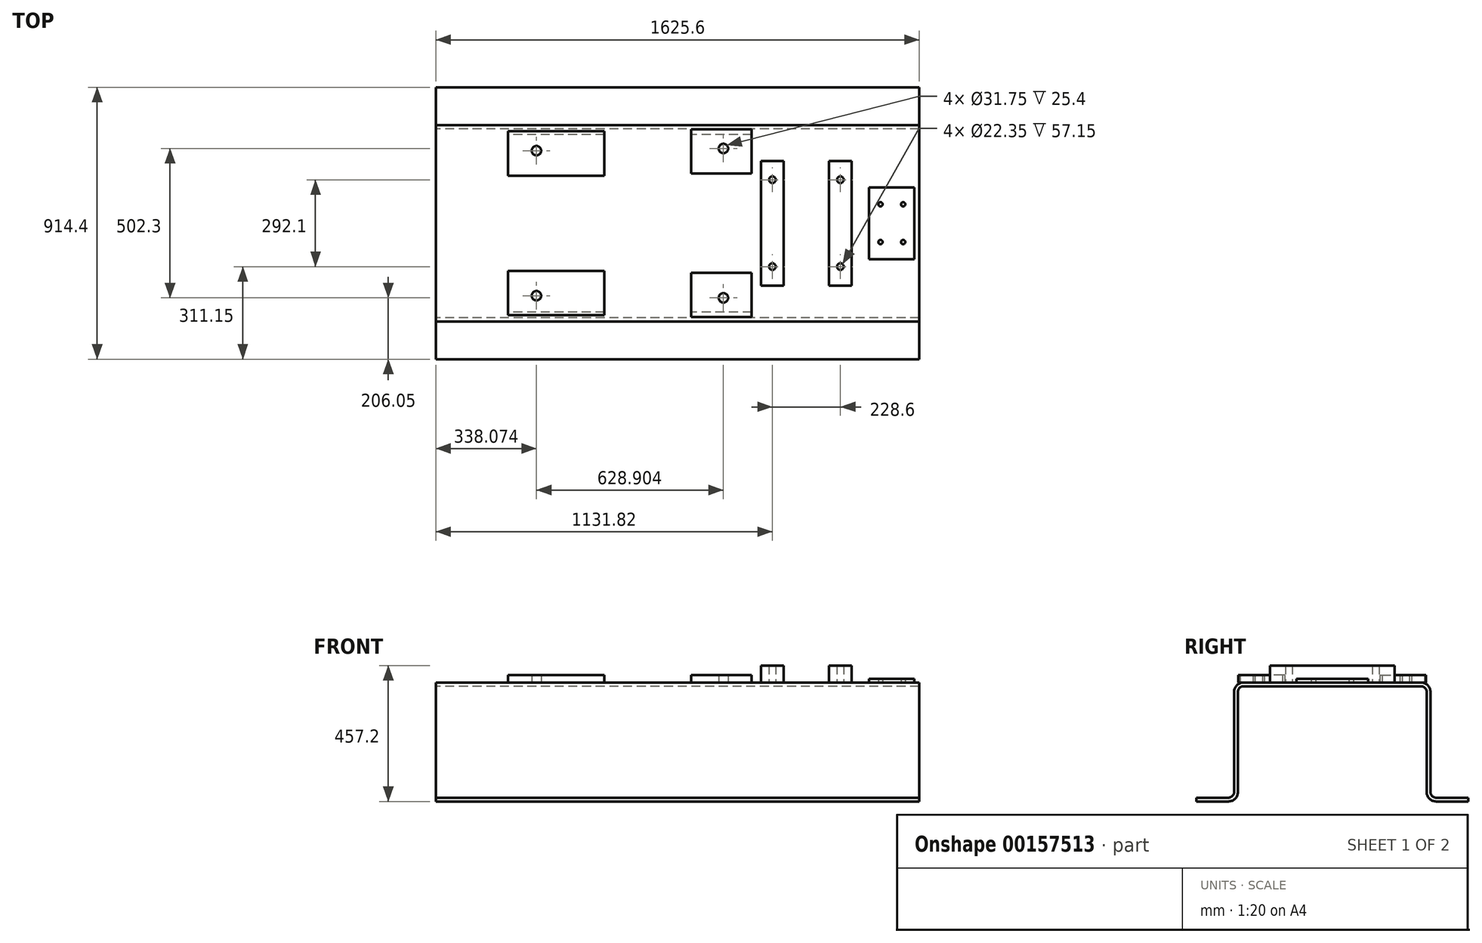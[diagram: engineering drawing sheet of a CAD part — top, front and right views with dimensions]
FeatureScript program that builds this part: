
annotation { "Feature Type Name" : "Feature", "Feature Type Description" : "" }
export const myFeature = defineFeature(function(context is Context, id is Id, definition is map)
    precondition{}
    {
        {
            var Q0;
            Q0=qCreatedBy(makeId("Right.planeOp"),FACE);
            var sketch = newSketch(context, id + "F0", { "sketchPlane" : qUnion([Q0])});
            skLineSegment(sketch, "E0", {"start": v(349.25, 0) * mm, "end": v(457.2, 0) * mm});
            skLineSegment(sketch, "E1.0", {"start": v(349.25, 12.7) * mm, "end": v(457.2, 12.7) * mm});
            skLineSegment(sketch, "E2.0", {"start": v(0, 400.05) * mm, "end": v(298.45, 400.05) * mm});
            skLineSegment(sketch, "E3", {"start": v(0, -167.8) * mm, "end": v(0, 400.05) * mm, "construction": true});
            skLineSegment(sketch, "E4.0", {"start": v(0, 387.35) * mm, "end": v(298.45, 387.35) * mm});
            skLineSegment(sketch, "E5.0", {"start": v(330.2, 31.75) * mm, "end": v(330.2, 368.3) * mm});
            skLineSegment(sketch, "E6.0", {"start": v(317.5, 31.75) * mm, "end": v(317.5, 368.3) * mm});
            skArc(sketch, "E7.filletArc", {"start": v(330.2, 31.75) * mm, "mid": v(335.78, 18.28) * mm, "end": v(349.25, 12.7) * mm});
            skArc(sketch, "E8.filletArc", {"start": v(317.5, 368.3) * mm, "mid": v(311.92, 381.77) * mm, "end": v(298.45, 387.35) * mm});
            skArc(sketch, "E9.filletArc", {"start": v(330.2, 368.3) * mm, "mid": v(320.9, 390.75) * mm, "end": v(298.45, 400.05) * mm});
            skPoint(sketch, "E10.newPointA", {"position": v(-457.2, 0) * mm});
            skArc(sketch, "E10.filletArc", {"start": v(317.5, 31.75) * mm, "mid": v(326.8, 9.3) * mm, "end": v(349.25, 0) * mm});
            skLineSegment(sketch, "E11", {"start": v(457.2, 12.7) * mm, "end": v(457.2, 0) * mm});
            skLineSegment(sketch, "E12.MirrorCS", {"start": v(-457.2, 12.7) * mm, "end": v(-457.2, 0) * mm});
            skArc(sketch, "E13.MirrorCS", {"start": v(-330.2, 368.3) * mm, "mid": v(-320.9, 390.75) * mm, "end": v(-298.45, 400.05) * mm});
            skArc(sketch, "E14.MirrorCS", {"start": v(-330.2, 31.75) * mm, "mid": v(-335.78, 18.28) * mm, "end": v(-349.25, 12.7) * mm});
            skArc(sketch, "E15.MirrorCS", {"start": v(-317.5, 368.3) * mm, "mid": v(-311.92, 381.77) * mm, "end": v(-298.45, 387.35) * mm});
            skArc(sketch, "E16.MirrorCS", {"start": v(-317.5, 31.75) * mm, "mid": v(-326.8, 9.3) * mm, "end": v(-349.25, 0) * mm});
            skLineSegment(sketch, "E17.MirrorCS", {"start": v(-349.25, 0) * mm, "end": v(-457.2, 0) * mm});
            skLineSegment(sketch, "E18.MirrorCS", {"start": v(-349.25, 12.7) * mm, "end": v(-457.2, 12.7) * mm});
            skLineSegment(sketch, "E19.MirrorCS", {"start": v(0, 400.05) * mm, "end": v(-298.45, 400.05) * mm});
            skLineSegment(sketch, "E20.MirrorCS", {"start": v(0, 387.35) * mm, "end": v(-298.45, 387.35) * mm});
            skLineSegment(sketch, "E21.MirrorCS", {"start": v(-317.5, 31.75) * mm, "end": v(-317.5, 368.3) * mm});
            skLineSegment(sketch, "E22.MirrorCS", {"start": v(-330.2, 31.75) * mm, "end": v(-330.2, 368.3) * mm});
            skSolve(sketch);
        }
        {
            var Q0;
            Q0=qSketchRegion(id+"F0",true);
            extrude(context, id + "F1", {"entities" : qUnion([Q0]), "endBound" : BoundingType.SYMMETRIC, "depth" : 1625.6 * mm});
        }
        {
            var Q0;
            Q0=makeQuery(id+"F1.opExtrude","SWEPT_FACE",FACE,{"disambiguationData":[OSD([sQuery(id+"F0.wireOp",EDGE,"E2.0"),sQuery(id+"F0.wireOp",EDGE,"E19.MirrorCS")])]});
            var sketch = newSketch(context, id + "F2", { "sketchPlane" : qUnion([Q0])});
            skLineSegment(sketch, "E23.0", {"start": v(812.8, -298.45) * mm, "end": v(812.8, 298.45) * mm, "construction": true});
            skLineSegment(sketch, "E24.0", {"start": v(-1600.2, -987.8) * mm, "end": v(-1600.2, 298.45) * mm, "construction": true});
            skLineSegment(sketch, "E25.0", {"start": v(-1143, -987.8) * mm, "end": v(-1143, 298.45) * mm, "construction": true});
            skLineSegment(sketch, "E26.0", {"start": v(-160.27, -987.8) * mm, "end": v(-160.27, 298.45) * mm, "construction": true});
            skLineSegment(sketch, "E27.0", {"start": v(433.32, -987.8) * mm, "end": v(433.32, 298.45) * mm, "construction": true});
            skLineSegment(sketch, "E28.0", {"start": v(45.97, -987.8) * mm, "end": v(45.97, 298.45) * mm, "construction": true});
            skLineSegment(sketch, "E29.0", {"start": v(249.17, -987.8) * mm, "end": v(249.17, 298.45) * mm, "construction": true});
            skLineSegment(sketch, "E30.0", {"start": v(-246.13, -987.8) * mm, "end": v(-246.13, 298.45) * mm, "construction": true});
            skLineSegment(sketch, "E31.0", {"start": v(-569.98, -987.8) * mm, "end": v(-569.98, 298.45) * mm, "construction": true});
            skLineSegment(sketch, "E32.0", {"start": v(-958.44, -155.44) * mm, "end": v(1000.49, -178.16) * mm, "construction": true});
            skLineSegment(sketch, "E33.0", {"start": v(-960.13, -301.48) * mm, "end": v(998.8, -324.2) * mm, "construction": true});
            skLineSegment(sketch, "E34.bottom", {"start": v(-569.98, -159.94) * mm, "end": v(-246.13, -159.94) * mm});
            skLineSegment(sketch, "E34.top", {"start": v(-569.98, -309.76) * mm, "end": v(-246.13, -309.76) * mm});
            skLineSegment(sketch, "E34.left", {"start": v(-569.98, -159.94) * mm, "end": v(-569.98, -309.76) * mm});
            skLineSegment(sketch, "E34.right", {"start": v(-246.13, -159.94) * mm, "end": v(-246.13, -309.76) * mm});
            skLineSegment(sketch, "E35.bottom", {"start": v(45.97, -167.09) * mm, "end": v(249.17, -167.09) * mm});
            skLineSegment(sketch, "E35.top", {"start": v(45.97, -315.5) * mm, "end": v(249.17, -315.5) * mm});
            skLineSegment(sketch, "E35.left", {"start": v(45.97, -167.09) * mm, "end": v(45.97, -315.5) * mm});
            skLineSegment(sketch, "E35.right", {"start": v(249.17, -167.09) * mm, "end": v(249.17, -315.5) * mm});
            skLineSegment(sketch, "E36.0", {"start": v(-474.73, -987.8) * mm, "end": v(-474.73, 298.45) * mm, "construction": true});
            skLineSegment(sketch, "E37.0", {"start": v(154.18, -987.8) * mm, "end": v(154.18, 298.45) * mm, "construction": true});
            skLineSegment(sketch, "E38.0", {"start": v(-959.4, -238.24) * mm, "end": v(999.53, -260.95) * mm, "construction": true});
            skCircle(sketch, "E39", {"center": v(-474.73, -243.86) * mm, "radius": 15.88 * mm});
            skCircle(sketch, "E40", {"center": v(154.18, -251.15) * mm, "radius": 15.88 * mm});
            skLineSegment(sketch, "E41", {"start": v(-969.18, 0) * mm, "end": v(1017.58, 0) * mm, "construction": true});
            skPoint(sketch, "E41.startSnap0", {"position": v(-812.8, 0) * mm});
            skCircle(sketch, "E42.MirrorC", {"center": v(154.18, 251.15) * mm, "radius": 15.88 * mm});
            skCircle(sketch, "E43.MirrorC", {"center": v(-474.73, 243.86) * mm, "radius": 15.88 * mm});
            skLineSegment(sketch, "E44.MirrorCS", {"start": v(-246.13, 159.94) * mm, "end": v(-246.13, 309.76) * mm});
            skLineSegment(sketch, "E45.MirrorCS", {"start": v(45.97, 167.09) * mm, "end": v(249.17, 167.09) * mm});
            skLineSegment(sketch, "E46.MirrorCS", {"start": v(249.17, 167.09) * mm, "end": v(249.17, 315.5) * mm});
            skLineSegment(sketch, "E47.MirrorCS", {"start": v(45.97, 315.5) * mm, "end": v(249.17, 315.5) * mm});
            skLineSegment(sketch, "E48.MirrorCS", {"start": v(-569.98, 159.94) * mm, "end": v(-569.98, 309.76) * mm});
            skLineSegment(sketch, "E49.MirrorCS", {"start": v(-569.98, 309.76) * mm, "end": v(-246.13, 309.76) * mm});
            skLineSegment(sketch, "E50.MirrorCS", {"start": v(45.97, 167.09) * mm, "end": v(45.97, 315.5) * mm});
            skLineSegment(sketch, "E51.MirrorCS", {"start": v(-569.98, 159.94) * mm, "end": v(-246.13, 159.94) * mm});
            skSolve(sketch);
        }
        {
            var Q0;
            Q0=qSketchRegion(id+"F2",true);
            extrude(context, id + "F3", {"entities" : qUnion([Q0]), "operationType" : NewBodyOperationType.ADD, "depth" : 25.4 * mm});
        }
        {
            var Q0;
            {var subQ7=sQuery(id+"F0.wireOp",EDGE,"E19.MirrorCS");var subQ17=sQuery(id+"F0.wireOp",EDGE,"E9.filletArc");var subQ23=sQuery(id+"F0.wireOp",EDGE,"E2.0");Q0=makeQuery(id+"F3.boolean.opBoolean","SPLIT",FACE,{"disambiguationData":[TD([makeQuery(id+"F1.opExtrude","SWEPT_FACE",FACE,{"disambiguationData":[OSD([subQ17])]})])],"derivedFrom":makeQuery(id+"F1.opExtrude","SWEPT_FACE",FACE,{"disambiguationData":[OSD([subQ23,subQ7])]})});}
            var sketch = newSketch(context, id + "F4", { "sketchPlane" : qUnion([Q0])});
            skLineSegment(sketch, "E52.0", {"start": v(509.52, -209.55) * mm, "end": v(509.52, 209.55) * mm});
            skLineSegment(sketch, "E53.0", {"start": v(585.72, -209.55) * mm, "end": v(585.72, 209.55) * mm});
            skLineSegment(sketch, "E54.0", {"start": v(509.52, 209.55) * mm, "end": v(585.72, 209.55) * mm});
            skLineSegment(sketch, "E55.0", {"start": v(509.52, -209.55) * mm, "end": v(585.72, -209.55) * mm});
            skLineSegment(sketch, "E56.0", {"start": v(547.62, -987.8) * mm, "end": v(547.62, 298.45) * mm, "construction": true});
            skLineSegment(sketch, "E57.0", {"start": v(-969.18, 146.05) * mm, "end": v(1017.58, 146.05) * mm, "construction": true});
            skLineSegment(sketch, "E58.0", {"start": v(-969.18, -146.05) * mm, "end": v(1017.58, -146.05) * mm, "construction": true});
            skCircle(sketch, "E59", {"center": v(547.62, 146.05) * mm, "radius": 11.18 * mm});
            skCircle(sketch, "E60", {"center": v(547.62, -146.05) * mm, "radius": 11.18 * mm});
            skCircle(sketch, "E61.MirrorC", {"center": v(319.02, 146.05) * mm, "radius": 11.18 * mm});
            skCircle(sketch, "E62.MirrorC", {"center": v(319.02, -146.05) * mm, "radius": 11.18 * mm});
            skLineSegment(sketch, "E63.MirrorCS", {"start": v(357.12, -209.55) * mm, "end": v(357.12, 209.55) * mm});
            skLineSegment(sketch, "E64.MirrorCS", {"start": v(280.92, -209.55) * mm, "end": v(280.92, 209.55) * mm});
            skLineSegment(sketch, "E65.MirrorCS", {"start": v(357.12, 209.55) * mm, "end": v(280.92, 209.55) * mm});
            skLineSegment(sketch, "E66.MirrorCS", {"start": v(357.12, -209.55) * mm, "end": v(280.92, -209.55) * mm});
            skSolve(sketch);
        }
        {
            var Q0;
            Q0=qSketchRegion(id+"F4",true);
            extrude(context, id + "F5", {"entities" : qUnion([Q0]), "operationType" : NewBodyOperationType.ADD, "depth" : 57.15 * mm});
        }
        {
            var Q0;
            {var subQ14=sQuery(id+"F2.wireOp",EDGE,"E34.bottom");Q0=makeQuery(id+"F2.imprint","IMPRINT",FACE,{"disambiguationData":[TD([[makeQuery(id+"F2.imprint","IMPRINT",EDGE,{"derivedFrom":subQ14}),1.0]])]});}
            var sketch = newSketch(context, id + "F6", { "sketchPlane" : qUnion([Q0])});
            skLineSegment(sketch, "E67.0", {"start": v(812.8, -298.45) * mm, "end": v(812.8, 298.45) * mm, "construction": true});
            skLineSegment(sketch, "E68.0", {"start": v(796.8, -298.45) * mm, "end": v(796.8, 298.45) * mm, "construction": true});
            skLineSegment(sketch, "E69.0", {"start": v(644.4, -298.45) * mm, "end": v(644.4, 298.45) * mm, "construction": true});
            skLineSegment(sketch, "E70", {"start": v(0, 0) * mm, "end": v(952.88, 0) * mm, "construction": true});
            skLineSegment(sketch, "E71.0", {"start": v(0, 120.65) * mm, "end": v(952.88, 120.65) * mm, "construction": true});
            skLineSegment(sketch, "E72.0", {"start": v(0, -120.65) * mm, "end": v(952.88, -120.65) * mm, "construction": true});
            skLineSegment(sketch, "E73.bottom", {"start": v(644.4, 120.65) * mm, "end": v(796.8, 120.65) * mm});
            skLineSegment(sketch, "E73.top", {"start": v(644.4, -120.65) * mm, "end": v(796.8, -120.65) * mm});
            skLineSegment(sketch, "E73.left", {"start": v(644.4, 120.65) * mm, "end": v(644.4, -120.65) * mm});
            skLineSegment(sketch, "E73.right", {"start": v(796.8, 120.65) * mm, "end": v(796.8, -120.65) * mm});
            skLineSegment(sketch, "E74.0", {"start": v(0, 63.5) * mm, "end": v(952.88, 63.5) * mm, "construction": true});
            skLineSegment(sketch, "E75.MirrorCS", {"start": v(0, -63.5) * mm, "end": v(952.88, -63.5) * mm, "construction": true});
            skLineSegment(sketch, "E76.0", {"start": v(682.5, -987.8) * mm, "end": v(682.5, 298.45) * mm, "construction": true});
            skLineSegment(sketch, "E77.0", {"start": v(758.7, -987.8) * mm, "end": v(758.7, 298.45) * mm, "construction": true});
            skCircle(sketch, "E78", {"center": v(682.5, 63.5) * mm, "radius": 7.14 * mm});
            skCircle(sketch, "E79", {"center": v(758.7, 63.5) * mm, "radius": 7.14 * mm});
            skCircle(sketch, "E80", {"center": v(682.5, -63.5) * mm, "radius": 7.14 * mm});
            skCircle(sketch, "E81", {"center": v(758.7, -63.5) * mm, "radius": 7.14 * mm});
            skSolve(sketch);
        }
        {
            var Q0;
            Q0=qSketchRegion(id+"F6",true);
            extrude(context, id + "F7", {"entities" : qUnion([Q0]), "operationType" : NewBodyOperationType.ADD, "depth" : 12.7 * mm});
        }
    });
